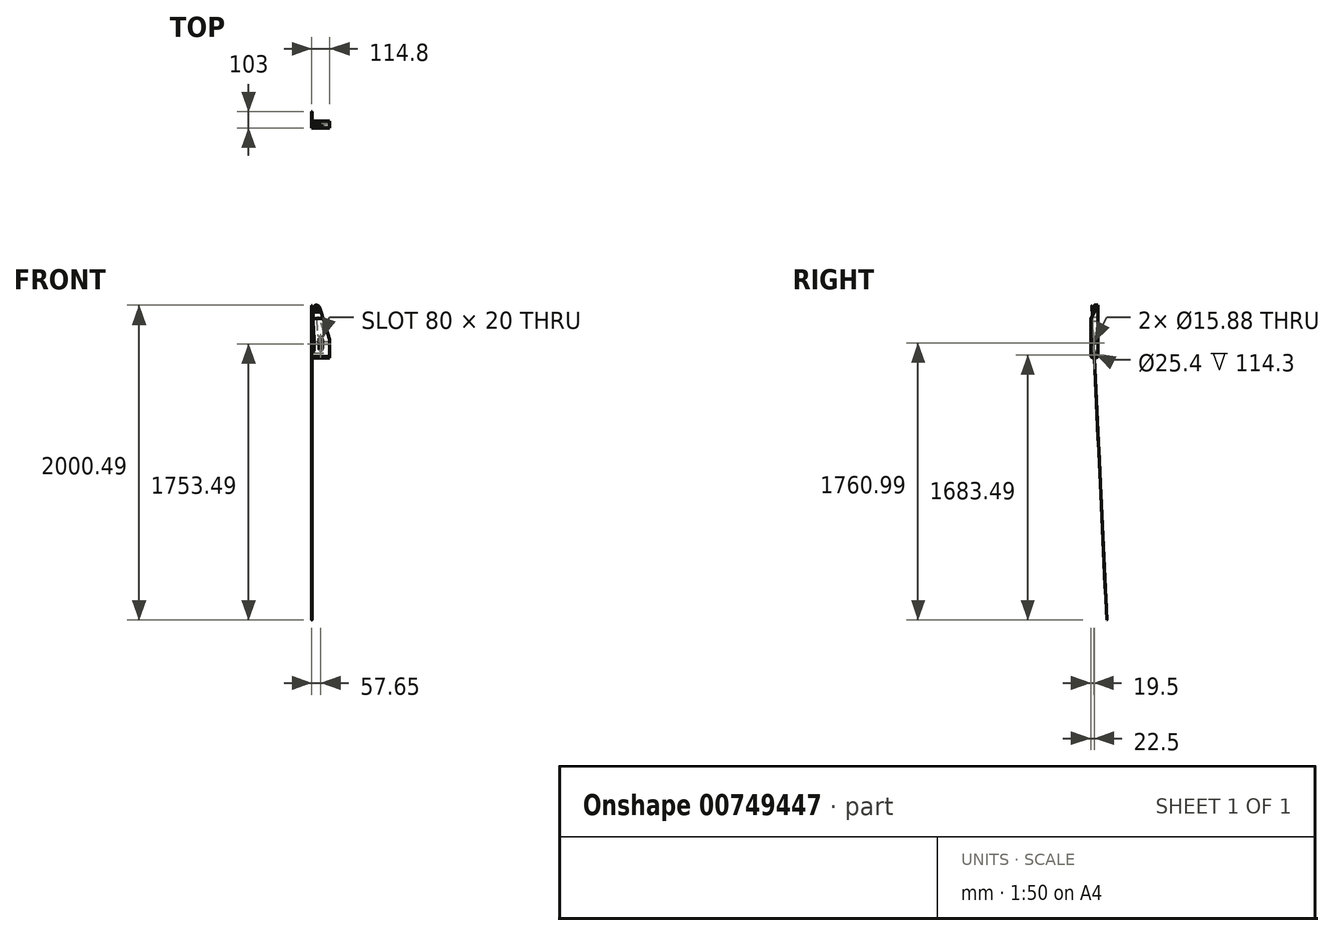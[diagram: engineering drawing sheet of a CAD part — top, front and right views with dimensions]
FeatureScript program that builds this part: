
annotation { "Feature Type Name" : "Feature", "Feature Type Description" : "" }
export const myFeature = defineFeature(function(context is Context, id is Id, definition is map)
    precondition{}
    {
        {
            var Q0;
            Q0=qCreatedBy(makeId("Front.planeOp"),FACE);
            var sketch = newSketch(context, id + "F0", { "sketchPlane" : qUnion([Q0])});
            skLineSegment(sketch, "E0", {"start": v(0, 0) * mm, "end": v(0, 40) * mm});
            skLineSegment(sketch, "E1", {"start": v(114.3, 0) * mm, "end": v(0, 0) * mm});
            skLineSegment(sketch, "E2", {"start": v(0, 40) * mm, "end": v(5, 40) * mm});
            skArc(sketch, "E3.filletArc", {"start": v(5, 40) * mm, "mid": v(12.07, 42.93) * mm, "end": v(15, 50) * mm});
            skCircle(sketch, "E4", {"center": v(30, 317) * mm, "radius": 2.5 * mm});
            skLineSegment(sketch, "E5", {"start": v(0, 20) * mm, "end": v(114.3, 20) * mm, "construction": true});
            skLineSegment(sketch, "E6", {"start": v(15, 50) * mm, "end": v(15, 120) * mm});
            skLineSegment(sketch, "E7", {"start": v(15, 120) * mm, "end": v(10, 237) * mm});
            skLineSegment(sketch, "E8", {"start": v(10, 237) * mm, "end": v(10, 317) * mm});
            skLineSegment(sketch, "E9", {"start": v(114.3, 0) * mm, "end": v(114.3, 120) * mm});
            skLineSegment(sketch, "E10", {"start": v(114.3, 120) * mm, "end": v(49.34, 322.1) * mm});
            skPoint(sketch, "E11.visualSharp", {"position": v(39.13, 353.86) * mm});
            skPoint(sketch, "E12.visualSharp", {"position": v(10, 337) * mm});
            skArc(sketch, "E13", {"start": v(10, 317) * mm, "mid": v(27.43, 336.83) * mm, "end": v(49.34, 322.1) * mm});
            skLineSegment(sketch, "E14.bottom", {"start": v(57.15, 130) * mm, "end": v(57.15, 130) * mm});
            skLineSegment(sketch, "E14.left", {"start": v(67.15, 120) * mm, "end": v(67.15, 60) * mm});
            skLineSegment(sketch, "E14.right", {"start": v(47.15, 120) * mm, "end": v(47.15, 60) * mm});
            skLineSegment(sketch, "E15", {"start": v(47.15, 40) * mm, "end": v(0, 40) * mm, "construction": true});
            skLineSegment(sketch, "E16", {"start": v(67.15, 40) * mm, "end": v(114.3, 40) * mm, "construction": true});
            skPoint(sketch, "E17.visualSharp", {"position": v(67.15, 130) * mm});
            skArc(sketch, "E17.filletArc", {"start": v(67.15, 120) * mm, "mid": v(64.22, 127.07) * mm, "end": v(57.15, 130) * mm});
            skPoint(sketch, "E18.visualSharp", {"position": v(47.15, 130) * mm});
            skArc(sketch, "E18.filletArc", {"start": v(57.15, 130) * mm, "mid": v(50.08, 127.07) * mm, "end": v(47.15, 120) * mm});
            skPoint(sketch, "E19.visualSharp", {"position": v(67.15, 40) * mm});
            skPoint(sketch, "E20.visualSharp", {"position": v(47.15, 40) * mm});
            skLineSegment(sketch, "E21", {"start": v(57.15, 50) * mm, "end": v(57.15, 50) * mm});
            skLineSegment(sketch, "E22", {"start": v(67.15, 40) * mm, "end": v(67.15, 50) * mm, "construction": true});
            skLineSegment(sketch, "E23", {"start": v(47.15, 50) * mm, "end": v(47.15, 40) * mm, "construction": true});
            skPoint(sketch, "E24.visualSharp", {"position": v(67.15, 50) * mm});
            skArc(sketch, "E24.filletArc", {"start": v(57.15, 50) * mm, "mid": v(64.22, 52.93) * mm, "end": v(67.15, 60) * mm});
            skPoint(sketch, "E25.visualSharp", {"position": v(47.15, 50) * mm});
            skArc(sketch, "E25.filletArc", {"start": v(47.15, 60) * mm, "mid": v(50.08, 52.93) * mm, "end": v(57.15, 50) * mm});
            skSolve(sketch);
        }
        {
            var Q0;
            Q0 = qSketchRegion(id + "F0", true);
            extrude(context, id + "F1", {"entities" : qUnion([Q0]), "depth" : 45 * mm, "offsetDistance" : 25 * mm});
        }
        {
            var Q0;
            Q0=makeQuery(id+"F1.opExtrude","SWEPT_FACE",FACE,{"disambiguationData":[OSD([sQuery(id+"F0.wireOp",EDGE,"E9")])]});
            var sketch = newSketch(context, id + "F2", { "sketchPlane" : qUnion([Q0])});
            skCircle(sketch, "E26", {"center": v(-22.5, 20) * mm, "radius": 12.7 * mm});
            skCircle(sketch, "E27", {"center": v(-25.5, 97.5) * mm, "radius": 7.94 * mm});
            skSolve(sketch);
        }
        {
            var Q0;
            Q0=makeQuery(id+"F2.imprint","IMPRINT",FACE,{"disambiguationData":[TD([[makeQuery(id+"F2.imprint","IMPRINT",EDGE,{"derivedFrom":sQuery(id+"F2.wireOp",EDGE,"E27")}),1.0]])]});
            var Q1;
            Q1=makeQuery(id+"F2.imprint","IMPRINT",FACE,{"disambiguationData":[TD([[makeQuery(id+"F2.imprint","IMPRINT",EDGE,{"derivedFrom":sQuery(id+"F2.wireOp",EDGE,"E26")}),1.0]])]});
            extrude(context, id + "F3", {"entities" : qUnion([Q0, Q1]), "operationType" : NewBodyOperationType.REMOVE, "endBound" : BoundingType.THROUGH_ALL, "oppositeDirection" : true, "depth" : 25 * mm, "offsetDistance" : 25 * mm});
        }
        {
            var Q0;
            Q0=makeQuery(id+"F1.opExtrude","CAP_FACE",FACE,{"disambiguationData":[OSD([sQuery(id+"F0.wireOp",EDGE,"E0"),sQuery(id+"F0.wireOp",EDGE,"E1"),sQuery(id+"F0.wireOp",EDGE,"E2"),sQuery(id+"F0.wireOp",EDGE,"E3.filletArc"),sQuery(id+"F0.wireOp",EDGE,"E4"),sQuery(id+"F0.wireOp",EDGE,"E6"),sQuery(id+"F0.wireOp",EDGE,"E7"),sQuery(id+"F0.wireOp",EDGE,"E8"),sQuery(id+"F0.wireOp",EDGE,"E9"),sQuery(id+"F0.wireOp",EDGE,"E10"),sQuery(id+"F0.wireOp",EDGE,"E13"),sQuery(id+"F0.wireOp",EDGE,"E14.left"),sQuery(id+"F0.wireOp",EDGE,"E14.right"),sQuery(id+"F0.wireOp",EDGE,"E17.filletArc"),sQuery(id+"F0.wireOp",EDGE,"E18.filletArc"),sQuery(id+"F0.wireOp",EDGE,"E19.filletArc"),sQuery(id+"F0.wireOp",EDGE,"E20.filletArc")])],"isStart":true});
            var sketch = newSketch(context, id + "F4", { "sketchPlane" : qUnion([Q0])});
            skLineSegment(sketch, "E28", {"start": v(-80.56, 153.06) * mm, "end": v(-48.42, 253.06) * mm});
            skLineSegment(sketch, "E29", {"start": v(-37.83, 261.34) * mm, "end": v(-37.83, 261.34) * mm});
            skLineSegment(sketch, "E30", {"start": v(-31.48, 249.57) * mm, "end": v(-35.76, 149.57) * mm});
            skLineSegment(sketch, "E31", {"start": v(-45.75, 140) * mm, "end": v(-71.04, 140) * mm});
            skPoint(sketch, "E32.visualSharp", {"position": v(-84.76, 140) * mm});
            skArc(sketch, "E32.filletArc", {"start": v(-80.56, 153.06) * mm, "mid": v(-79.13, 144.1) * mm, "end": v(-71.04, 140) * mm});
            skPoint(sketch, "E33.visualSharp", {"position": v(-36.17, 140) * mm});
            skArc(sketch, "E33.filletArc", {"start": v(-45.75, 140) * mm, "mid": v(-38.83, 142.78) * mm, "end": v(-35.76, 149.57) * mm});
            skLineSegment(sketch, "E34", {"start": v(-41.47, 260) * mm, "end": v(-38.9, 260) * mm});
            skPoint(sketch, "E35.visualSharp", {"position": v(-46.2, 260) * mm});
            skArc(sketch, "E35.filletArc", {"start": v(-38.9, 260) * mm, "mid": v(-44.8, 258.08) * mm, "end": v(-48.42, 253.06) * mm});
            skPoint(sketch, "E36.visualSharp", {"position": v(-31.04, 260) * mm});
            skArc(sketch, "E36.filletArc", {"start": v(-31.48, 249.57) * mm, "mid": v(-34.25, 256.92) * mm, "end": v(-41.47, 260) * mm});
            skSolve(sketch);
        }
        {
            var Q0;
            Q0=makeQuery(id+"F4.imprint","IMPRINT",FACE,{"disambiguationData":[TD([[makeQuery(id+"F4.imprint","IMPRINT",EDGE,{"derivedFrom":sQuery(id+"F4.wireOp",EDGE,"E28")}),-1.0]])]});
            extrude(context, id + "F5", {"entities" : qUnion([Q0]), "operationType" : NewBodyOperationType.REMOVE, "oppositeDirection" : true, "depth" : 35 * mm, "offsetDistance" : 25 * mm});
        }
        {
            var Q0;
            Q0=makeQuery(id+"F1.opExtrude","SWEPT_FACE",FACE,{"disambiguationData":[OSD([sQuery(id+"F0.wireOp",EDGE,"E0")])]});
            var sketch = newSketch(context, id + "F6", { "sketchPlane" : qUnion([Q0])});
            skLineSegment(sketch, "E37", {"start": v(22, 458.5) * mm, "end": v(22, 291.83) * mm});
            skLineSegment(sketch, "E38", {"start": v(22, 291.83) * mm, "end": v(75.72, 198.78) * mm});
            skLineSegment(sketch, "E39", {"start": v(75.72, 198.78) * mm, "end": v(75.72, 458.5) * mm});
            skLineSegment(sketch, "E40", {"start": v(75.72, 458.5) * mm, "end": v(22, 458.5) * mm});
            skSolve(sketch);
        }
        {
            var Q0;
            Q0 = qSketchRegion(id + "F6", true);
            extrude(context, id + "F7", {"entities" : qUnion([Q0]), "operationType" : NewBodyOperationType.REMOVE, "endBound" : BoundingType.THROUGH_ALL, "oppositeDirection" : true, "depth" : 25 * mm, "offsetDistance" : 25 * mm});
        }
        {
            var Q0;
            Q0=makeQuery(id+"F1.opExtrude","CAP_EDGE",EDGE,{"disambiguationData":[OSD([sQuery(id+"F0.wireOp",EDGE,"E1")])],"isStart":true});
            var Q1;
            Q1=makeQuery(id+"F1.opExtrude","CAP_EDGE",EDGE,{"disambiguationData":[OSD([sQuery(id+"F0.wireOp",EDGE,"E1")])],"isStart":false});
            chamfer(context, id + "F8", {"entities" : qUnion([Q0, Q1]), "width" : 10 * mm, "tangentPropagation" : true});
        }
        {
            var Q0;
            Q0=makeQuery(id+"F7.boolean.opBoolean","COPY",FACE,{"derivedFrom":makeQuery(id+"F7.opExtrude","SWEPT_FACE",FACE,{"disambiguationData":[OSD([sQuery(id+"F6.wireOp",EDGE,"E37")])]})});
            var sketch = newSketch(context, id + "F9", { "sketchPlane" : qUnion([Q0])});
            skCircle(sketch, "E41", {"center": v(30, 317) * mm, "radius": 8.15 * mm});
            skSolve(sketch);
        }
        {
            var Q0;
            Q0 = qSketchRegion(id + "F9", true);
            extrude(context, id + "F10", {"entities" : qUnion([Q0]), "operationType" : NewBodyOperationType.REMOVE, "oppositeDirection" : true, "depth" : 25 * mm, "offsetDistance" : 25 * mm, "hasDraft" : true, "draftAngle" : 5.72 * degree, "draftPullDirection" : true});
        }
        {
            var Q0;
            Q0=makeQuery(id+"F1.opExtrude","SWEPT_FACE",FACE,{"disambiguationData":[OSD([sQuery(id+"F0.wireOp",EDGE,"E0")])]});
            var sketch = newSketch(context, id + "F11", { "sketchPlane" : qUnion([Q0])});
            skLineSegment(sketch, "E42", {"start": v(22.5, 20) * mm, "end": v(37.32, 334.29) * mm});
            skSolve(sketch);
        }
        {
            var Q0;
            Q0=sQuery(id+"F11.wireOp",VERTEX,"E42.end");
            var Q1;
            Q1=sQuery(id+"F11.wireOp",EDGE,"E42");
            cPlane(context, id + "F12", {"entities" : qUnion([Q0, Q1]), "cplaneType" : CPlaneType.LINE_POINT, "offset" : 25 * mm, "width" : 150 * mm, "height" : 150 * mm});
        }
        {
            var Q0;
            Q0=qCreatedBy(id+"F12.planeOp",FACE);
            var sketch = newSketch(context, id + "F13", { "sketchPlane" : qUnion([Q0])});
            skCircle(sketch, "E43", {"center": v(0, -20.92) * mm, "radius": 0.5 * mm});
            skSolve(sketch);
        }
        {
            var Q0;
            Q0 = qSketchRegion(id + "F13", true);
            extrude(context, id + "F14", {"entities" : qUnion([Q0]), "operationType" : NewBodyOperationType.ADD, "oppositeDirection" : true, "depth" : 2000 * mm, "offsetDistance" : 25 * mm});
        }
    });
